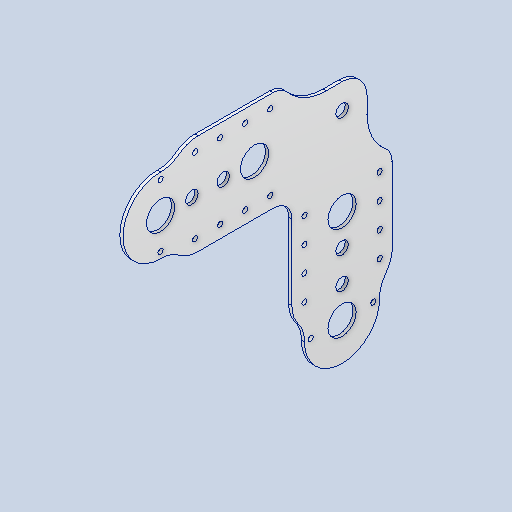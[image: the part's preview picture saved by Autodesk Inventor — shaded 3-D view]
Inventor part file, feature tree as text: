
AUTODESK INVENTOR PART (.ipt)
format: ipt  version: 2025.1 (Build 291241020, 241B)  size: 251,392 bytes
history: native  units: in
note: dims shown in document units (in); Inventor stores cm internally (conversion verified against a paired STEP export)
features: fillet x3, sketch x2, extrude x1
ambient origin geometry x8: Origin, YZ Plane, XZ Plane, XY Plane, X Axis, Y Axis, Z Axis, Center Point
bodies: Solid1 (feature_tree)
feature tree (6):
  extrude  "Extrusion1"  Depth=4.0in
  fillet  "Fillet1"  Radius=1.125in
  fillet  "Fillet2"  Radius=0.5in
  fillet  "Fillet3"  Radius=0.5in
  sketch  "Sketch Rectangular Pattern1"  dims[d0=4.0in d1=6.0in d2=1.125in d3=0.5in d4=0.5in]
  sketch  "Sketch Circular Pattern1"  dims[d5=1.125in d6=1.25in d7=1.25in d8=1.25in d9=0.2087in d10=0.5in d11=0.5in d12=2.3622in d14=1.0in d15=0.7874in d17=3.0in d20=0.125in d21=0.0in d22=0.5in d24=7.2441in d25=1.0in d26=2.0in d27=135.0deg d28=2.0in d29=1.0in d30=0.75in d31=2.0in d32=3.0in d33=1.25in d34=1.25in d35=0.75in d36=0.75in d37=0.7874in d39=90.0deg d41=1.25in d23=0.0344in]
